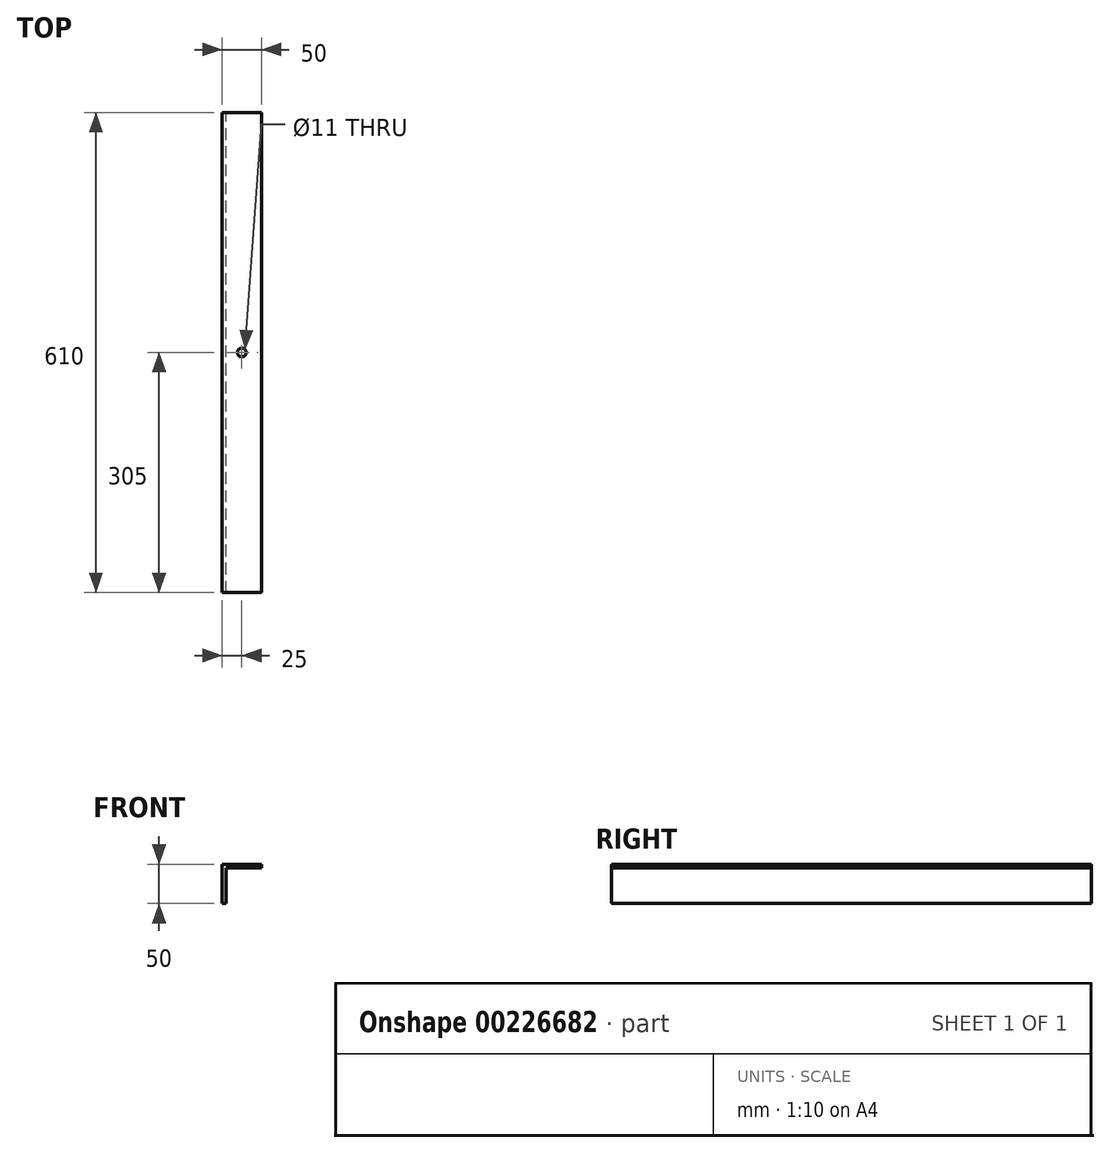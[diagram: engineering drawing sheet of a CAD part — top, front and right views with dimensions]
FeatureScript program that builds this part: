
annotation { "Feature Type Name" : "Feature", "Feature Type Description" : "" }
export const myFeature = defineFeature(function(context is Context, id is Id, definition is map)
    precondition{}
    {
        {
            var Q0;
            Q0=qCreatedBy(makeId("Front.planeOp"),FACE);
            var sketch = newSketch(context, id + "F0", { "sketchPlane" : qUnion([Q0])});
            skLineSegment(sketch, "E0", {"start": v(0, 0) * mm, "end": v(0, -50) * mm});
            skLineSegment(sketch, "E1", {"start": v(0, -50) * mm, "end": v(5, -50) * mm});
            skLineSegment(sketch, "E2", {"start": v(5, -50) * mm, "end": v(5, -5) * mm});
            skLineSegment(sketch, "E3", {"start": v(5, -5) * mm, "end": v(50, -5) * mm});
            skLineSegment(sketch, "E4", {"start": v(50, -5) * mm, "end": v(50, 0) * mm});
            skLineSegment(sketch, "E5", {"start": v(0, 0) * mm, "end": v(50, 0) * mm});
            skSolve(sketch);
        }
        {
            var Q0;
            Q0=makeQuery(id+"F0.imprint","IMPRINT",FACE,{"disambiguationData":[TD([[makeQuery(id+"F0.imprint","IMPRINT",EDGE,{"derivedFrom":sQuery(id+"F0.wireOp",EDGE,"E0")}),1.0]])]});
            extrude(context, id + "F1", {"entities" : qUnion([Q0]), "depth" : 610 * mm});
        }
        {
            var Q0;
            Q0=makeQuery(id+"F1.opExtrude","SWEPT_FACE",FACE,{"disambiguationData":[OSD([sQuery(id+"F0.wireOp",EDGE,"E5")])]});
            var sketch = newSketch(context, id + "F2", { "sketchPlane" : qUnion([Q0])});
            skCircle(sketch, "E6", {"center": v(25, -305) * mm, "radius": 5.5 * mm});
            skSolve(sketch);
        }
        {
            var Q0;
            Q0=makeQuery(id+"F2.imprint","IMPRINT",FACE,{"disambiguationData":[TD([[makeQuery(id+"F2.imprint","IMPRINT",EDGE,{"derivedFrom":sQuery(id+"F2.wireOp",EDGE,"E6")}),1.0]])]});
            extrude(context, id + "F3", {"entities" : qUnion([Q0]), "operationType" : NewBodyOperationType.REMOVE, "oppositeDirection" : true, "depth" : 25 * mm});
        }
    });
